# Revit family: Toilet-Floor_Mount-KOHLER-KARING-K-77780T_1
name_source: partatom
category: Plumbing Fixtures
revit_build: Autodesk Revit 2017 (Build: 20160225_1515(x64)
units: mm (PartAtom-declared; Revit-internal decimal feet)

## family parameters
Cut with Voids When Loaded = No
Host = Face
OmniClass Number = 23.31.19.00
OmniClass Title = Toilets
Part Type = Normal
Room Calculation Point = No
Round Connector Dimension = Use Diameter
Shared = No

## types (2) — shared parameters
ADA Compliant = No
Apparent Load = 2200 VA
Assembly Code = D2010100
Bowl Heigth = 15 3/8"
CW Connection = Yes
Cold Water Inlet = Cold Water Inlet
Date Modified = 06/25/2021
Default Elevation = 0"
Electrical Connector = Yes
Electrical Note = Connect only to dedicated 220V~, 50 Hz, 10A circuit protected by Ground-Fault Circuit-Interrupters
(GFCI’s) or Earth-Leakage Circuit-Breakers (ELCB’s).
Finish = Kohler-Vitreous_China-0-White
Flow Rate = 0 GPM
Flush Rate- GPF = 1.07 GPF
Flush Rate- LPF = 4.0 LPF
HW Connection = No
Height = 20 3/4"
Hot Water Inlet = Hot Water Inlet
Length = 27 3/4"
Manufacturer = KOHLER Co.
Master Format 2014 = 22 42 13.13
Master Format 2014 Name = Residential Water Closets
Material = Vitreous China
Pressure = 0.00 psi
Product Name = KARING
Rough-In = 12"
Seat Included = Yes
URL = http://www.kohler.com.cn
Vent Connection = No
Voltage = 220 V
Waste Connection = Yes
Waste Water Outlet = Waste Water Outlet
WaterSense Certified = No
Width = 17 3/4"

## per-type parameters (varying)
| type | Description | Model | Product Documentation Link | Product Page URL | Type |
| Deluxe Edition,0-White | KARING 2.0 Xinyue 2.0 Smart Toilet (Deluxe Edition) | K-77780T-0 | http://files.kohler.com.cn | http://www.kohler.com.cn | 1 |
| Cloud Version,0-White | Xinyue 2.0 smart toilet (cloud smart version) | K-77780T-XP-0 | https://files.kohler.com.cn | https://www.kohler.com.cn | 2 |

## geometry (parser evidence)
native form markers: Sweep x6
no freeform markers — native parametric forms only
